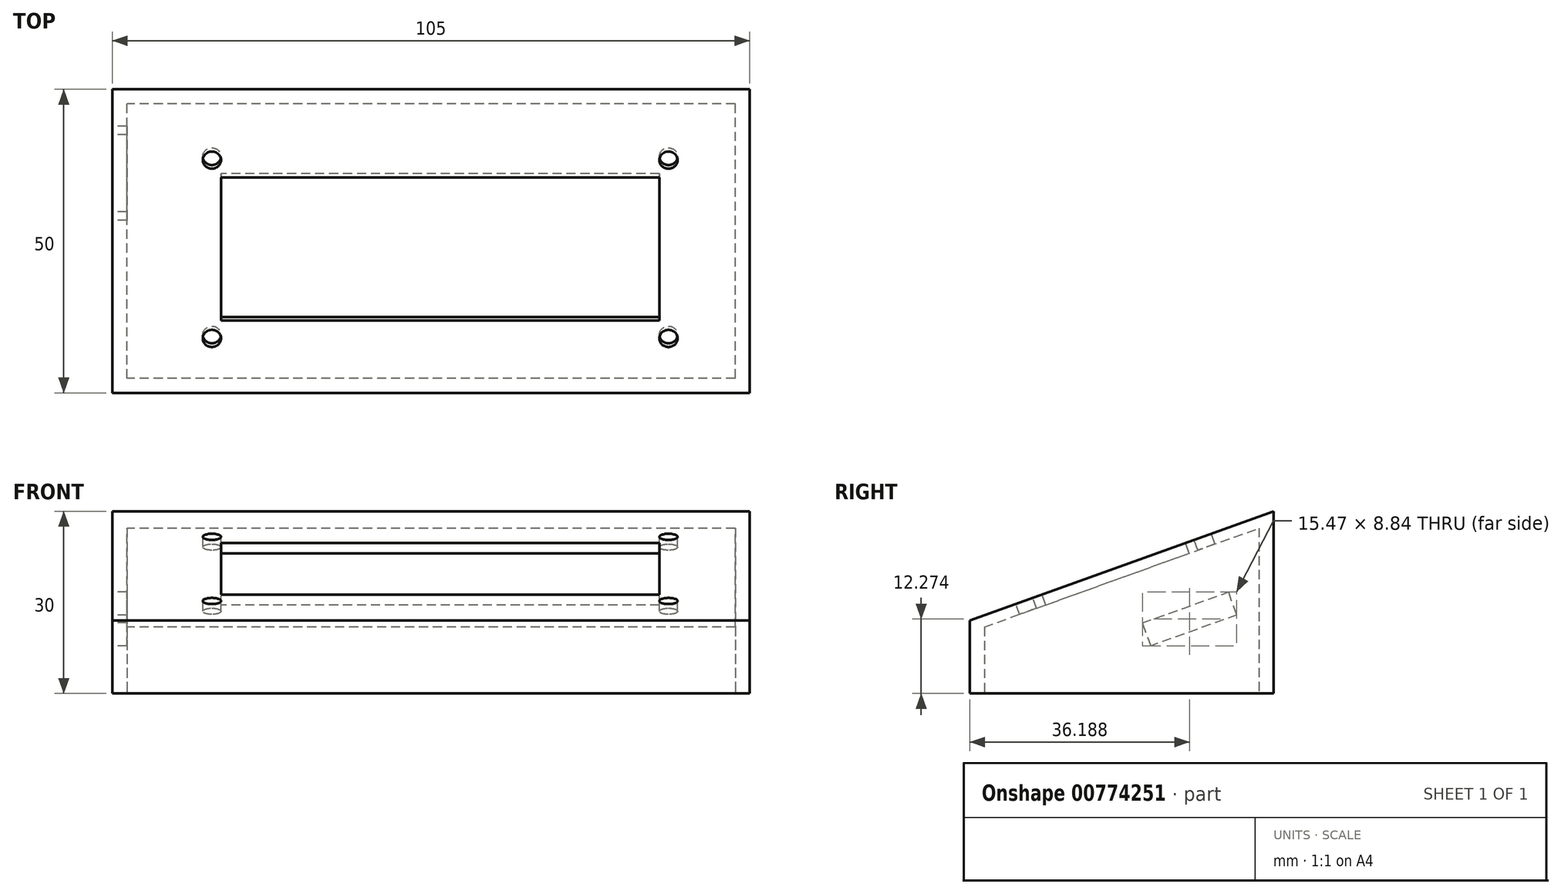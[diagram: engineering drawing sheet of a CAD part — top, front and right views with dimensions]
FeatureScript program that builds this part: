
annotation { "Feature Type Name" : "Feature", "Feature Type Description" : "" }
export const myFeature = defineFeature(function(context is Context, id is Id, definition is map)
    precondition{}
    {
        {
            var Q0;
            Q0=qCreatedBy(makeId("Top.planeOp"),FACE);
            var sketch = newSketch(context, id + "F0", { "sketchPlane" : qUnion([Q0])});
            skLineSegment(sketch, "E0.bottom", {"start": v(-52.5, 25) * mm, "end": v(52.5, 25) * mm});
            skLineSegment(sketch, "E0.top", {"start": v(-52.5, -25) * mm, "end": v(52.5, -25) * mm});
            skLineSegment(sketch, "E0.left", {"start": v(-52.5, 25) * mm, "end": v(-52.5, -25) * mm});
            skLineSegment(sketch, "E0.right", {"start": v(52.5, 25) * mm, "end": v(52.5, -25) * mm});
            skPoint(sketch, "E0.middle", {"position": v(0, 0) * mm});
            skLineSegment(sketch, "E1.0", {"start": v(-50.1, 22.6) * mm, "end": v(50.1, 22.6) * mm});
            skLineSegment(sketch, "E1.1", {"start": v(-50.1, 22.6) * mm, "end": v(-50.1, -22.6) * mm});
            skLineSegment(sketch, "E1.2", {"start": v(-50.1, -22.6) * mm, "end": v(50.1, -22.6) * mm});
            skLineSegment(sketch, "E1.3", {"start": v(50.1, 22.6) * mm, "end": v(50.1, -22.6) * mm});
            skCircle(sketch, "E2", {"center": v(56, 0) * mm, "radius": 1.5 * mm});
            skLineSegment(sketch, "E3.bottom", {"start": v(52.5, 4) * mm, "end": v(56, 4) * mm});
            skLineSegment(sketch, "E3.top", {"start": v(52.5, -4) * mm, "end": v(56, -4) * mm});
            skLineSegment(sketch, "E3.left", {"start": v(52.5, 4) * mm, "end": v(52.5, -4) * mm});
            skArc(sketch, "E4", {"start": v(56, 4) * mm, "mid": v(60, 0) * mm, "end": v(56, -4) * mm});
            skLineSegment(sketch, "E5", {"start": v(56, 4) * mm, "end": v(56, -4) * mm, "construction": true});
            skLineSegment(sketch, "E6.MirrorCS", {"start": v(-52.5, 4) * mm, "end": v(-56, 4) * mm});
            skArc(sketch, "E7.MirrorCS", {"start": v(-56, 4) * mm, "mid": v(-60, 0) * mm, "end": v(-56, -4) * mm});
            skLineSegment(sketch, "E8.MirrorCS", {"start": v(-52.5, 4) * mm, "end": v(-52.5, -4) * mm});
            skLineSegment(sketch, "E9.MirrorCS", {"start": v(-56, 4) * mm, "end": v(-56, -4) * mm, "construction": true});
            skCircle(sketch, "E10.MirrorC", {"center": v(-56, 0) * mm, "radius": 1.5 * mm});
            skLineSegment(sketch, "E11.MirrorCS", {"start": v(-52.5, -4) * mm, "end": v(-56, -4) * mm});
            skSolve(sketch);
        }
        {
            var Q0;
            Q0=makeQuery(id+"F0.imprint","IMPRINT",FACE,{"disambiguationData":[TD([[makeQuery(id+"F0.imprint","IMPRINT",EDGE,{"derivedFrom":sQuery(id+"F0.wireOp",EDGE,"E0.bottom")}),-1.0]])]});
            extrude(context, id + "F1", {"entities" : qUnion([Q0]), "depth" : 30 * mm, "offsetDistance" : 25 * mm});
        }
        {
            var Q0;
            Q0=makeQuery(id+"F1.opExtrude","SWEPT_FACE",FACE,{"disambiguationData":[OSD([sQuery(id+"F0.wireOp",EDGE,"E0.right")])]});
            var sketch = newSketch(context, id + "F2", { "sketchPlane" : qUnion([Q0])});
            skLineSegment(sketch, "E12", {"start": v(25, 30) * mm, "end": v(-25, 12) * mm});
            skLineSegment(sketch, "E13", {"start": v(-25, 12) * mm, "end": v(-25, 30) * mm});
            skLineSegment(sketch, "E14", {"start": v(-25, 30) * mm, "end": v(25, 30) * mm});
            skSolve(sketch);
        }
        {
            var Q0;
            Q0=makeQuery(id+"F2.imprint","IMPRINT",FACE,{"disambiguationData":[TD([[makeQuery(id+"F2.imprint","IMPRINT",EDGE,{"derivedFrom":sQuery(id+"F2.wireOp",EDGE,"E12")}),-1.0]])]});
            extrude(context, id + "F3", {"entities" : qUnion([Q0]), "operationType" : NewBodyOperationType.REMOVE, "endBound" : BoundingType.THROUGH_ALL, "oppositeDirection" : true, "depth" : 25 * mm, "offsetDistance" : 25 * mm});
        }
        {
            var Q0;
            Q0=makeQuery(id+"F3.boolean.opBoolean","COPY",FACE,{"derivedFrom":makeQuery(id+"F3.opExtrude","SWEPT_FACE",FACE,{"disambiguationData":[OSD([sQuery(id+"F2.wireOp",EDGE,"E12")])]})});
            var sketch = newSketch(context, id + "F4", { "sketchPlane" : qUnion([Q0])});
            skLineSegment(sketch, "E15", {"start": v(52.6, 33.68) * mm, "end": v(52.6, -19.3) * mm});
            skLineSegment(sketch, "E16", {"start": v(-52.6, 33.68) * mm, "end": v(-52.6, -19.3) * mm});
            skLineSegment(sketch, "E17.bottom", {"start": v(-34.6, 18.3) * mm, "end": v(37.6, 18.3) * mm});
            skLineSegment(sketch, "E17.top", {"start": v(-34.6, -6.8) * mm, "end": v(37.6, -6.8) * mm});
            skLineSegment(sketch, "E17.left", {"start": v(-34.6, 18.3) * mm, "end": v(-34.6, -6.8) * mm});
            skCircle(sketch, "E18", {"center": v(-36.1, -9.9) * mm, "radius": 1.5 * mm});
            skCircle(sketch, "E19.0.1.0", {"center": v(-36.1, 21.3) * mm, "radius": 1.5 * mm});
            skCircle(sketch, "E19.1.0.0", {"center": v(39.1, -9.9) * mm, "radius": 1.5 * mm});
            skCircle(sketch, "E19.1.1.0", {"center": v(39.1, 21.3) * mm, "radius": 1.5 * mm});
            skLineSegment(sketch, "E20", {"start": v(37.6, 18.3) * mm, "end": v(37.6, -6.8) * mm});
            skLineSegment(sketch, "E21", {"start": v(-52.6, -19.3) * mm, "end": v(52.6, -19.3) * mm});
            skLineSegment(sketch, "E22", {"start": v(52.6, 33.68) * mm, "end": v(-52.6, 33.68) * mm});
            skLineSegment(sketch, "E23", {"start": v(0, 33.68) * mm, "end": v(0, -19.3) * mm, "construction": true});
            skLineSegment(sketch, "E24", {"start": v(52.6, 7.19) * mm, "end": v(-52.6, 7.19) * mm, "construction": true});
            skLineSegment(sketch, "E25.0", {"start": v(-50.2, -16.9) * mm, "end": v(50.2, -16.9) * mm});
            skLineSegment(sketch, "E25.1", {"start": v(-50.2, 31.28) * mm, "end": v(-50.2, -16.9) * mm});
            skLineSegment(sketch, "E25.2", {"start": v(50.2, 31.28) * mm, "end": v(-50.2, 31.28) * mm});
            skLineSegment(sketch, "E25.3", {"start": v(50.2, 31.28) * mm, "end": v(50.2, -16.9) * mm});
            skSolve(sketch);
        }
        {
            var Q0;
            Q0=makeQuery(id+"F1.opExtrude","SWEPT_FACE",FACE,{"disambiguationData":[OSD([sQuery(id+"F0.wireOp",EDGE,"E0.left")])]});
            var sketch = newSketch(context, id + "F5", { "sketchPlane" : qUnion([Q0])});
            skLineSegment(sketch, "E26", {"start": v(-25, 30) * mm, "end": v(25, 12) * mm});
            skLineSegment(sketch, "E27", {"start": v(-25, 28.09) * mm, "end": v(25, 10.09) * mm});
            skLineSegment(sketch, "E28", {"start": v(-25, 30) * mm, "end": v(-25, 28.09) * mm});
            skLineSegment(sketch, "E29", {"start": v(25, 12) * mm, "end": v(25, 10.09) * mm});
            skLineSegment(sketch, "E30", {"start": v(-17.57, 16.7) * mm, "end": v(-3.45, 11.62) * mm});
            skLineSegment(sketch, "E31", {"start": v(-3.45, 11.62) * mm, "end": v(-4.8, 7.85) * mm});
            skLineSegment(sketch, "E32", {"start": v(-4.8, 7.85) * mm, "end": v(-18.92, 12.93) * mm});
            skLineSegment(sketch, "E33", {"start": v(-18.92, 12.93) * mm, "end": v(-17.57, 16.7) * mm});
            skLineSegment(sketch, "E34", {"start": v(-25, 30) * mm, "end": v(-31.26, 12.6) * mm, "construction": true});
            skSolve(sketch);
        }
        {
            var Q0;
            Q0=makeQuery(id+"F5.imprint","IMPRINT",FACE,{"disambiguationData":[TD([[makeQuery(id+"F5.imprint","IMPRINT",EDGE,{"derivedFrom":sQuery(id+"F5.wireOp",EDGE,"E26")}),-1.0]])]});
            extrude(context, id + "F6", {"entities" : qUnion([Q0]), "operationType" : NewBodyOperationType.ADD, "oppositeDirection" : true, "depth" : 105 * mm, "offsetDistance" : 25 * mm});
        }
        {
            var Q0;
            Q0=makeQuery(id+"F4.imprint","IMPRINT",FACE,{"disambiguationData":[TD([[makeQuery(id+"F4.imprint","IMPRINT",EDGE,{"derivedFrom":sQuery(id+"F4.wireOp",EDGE,"E17.bottom")}),-1.0]])]});
            var Q1;
            Q1=makeQuery(id+"F4.imprint","IMPRINT",FACE,{"disambiguationData":[TD([[makeQuery(id+"F4.imprint","IMPRINT",EDGE,{"derivedFrom":sQuery(id+"F4.wireOp",EDGE,"E19.1.0.0")}),1.0]])]});
            var Q2;
            Q2=makeQuery(id+"F4.imprint","IMPRINT",FACE,{"disambiguationData":[TD([[makeQuery(id+"F4.imprint","IMPRINT",EDGE,{"derivedFrom":sQuery(id+"F4.wireOp",EDGE,"E19.1.1.0")}),1.0]])]});
            var Q3;
            Q3=makeQuery(id+"F4.imprint","IMPRINT",FACE,{"disambiguationData":[TD([[makeQuery(id+"F4.imprint","IMPRINT",EDGE,{"derivedFrom":sQuery(id+"F4.wireOp",EDGE,"E18")}),1.0]])]});
            var Q4;
            Q4=makeQuery(id+"F4.imprint","IMPRINT",FACE,{"disambiguationData":[TD([[makeQuery(id+"F4.imprint","IMPRINT",EDGE,{"derivedFrom":sQuery(id+"F4.wireOp",EDGE,"E19.0.1.0")}),1.0]])]});
            extrude(context, id + "F7", {"entities" : qUnion([Q0, Q1, Q2, Q3, Q4]), "operationType" : NewBodyOperationType.REMOVE, "oppositeDirection" : true, "depth" : 5 * mm, "offsetDistance" : 25 * mm});
        }
        {
            var Q0;
            Q0=makeQuery(id+"F5.imprint","IMPRINT",FACE,{"disambiguationData":[TD([[makeQuery(id+"F5.imprint","IMPRINT",EDGE,{"derivedFrom":sQuery(id+"F5.wireOp",EDGE,"E30")}),-1.0]])]});
            extrude(context, id + "F8", {"entities" : qUnion([Q0]), "operationType" : NewBodyOperationType.REMOVE, "oppositeDirection" : true, "depth" : 5 * mm, "offsetDistance" : 25 * mm});
        }
    });
